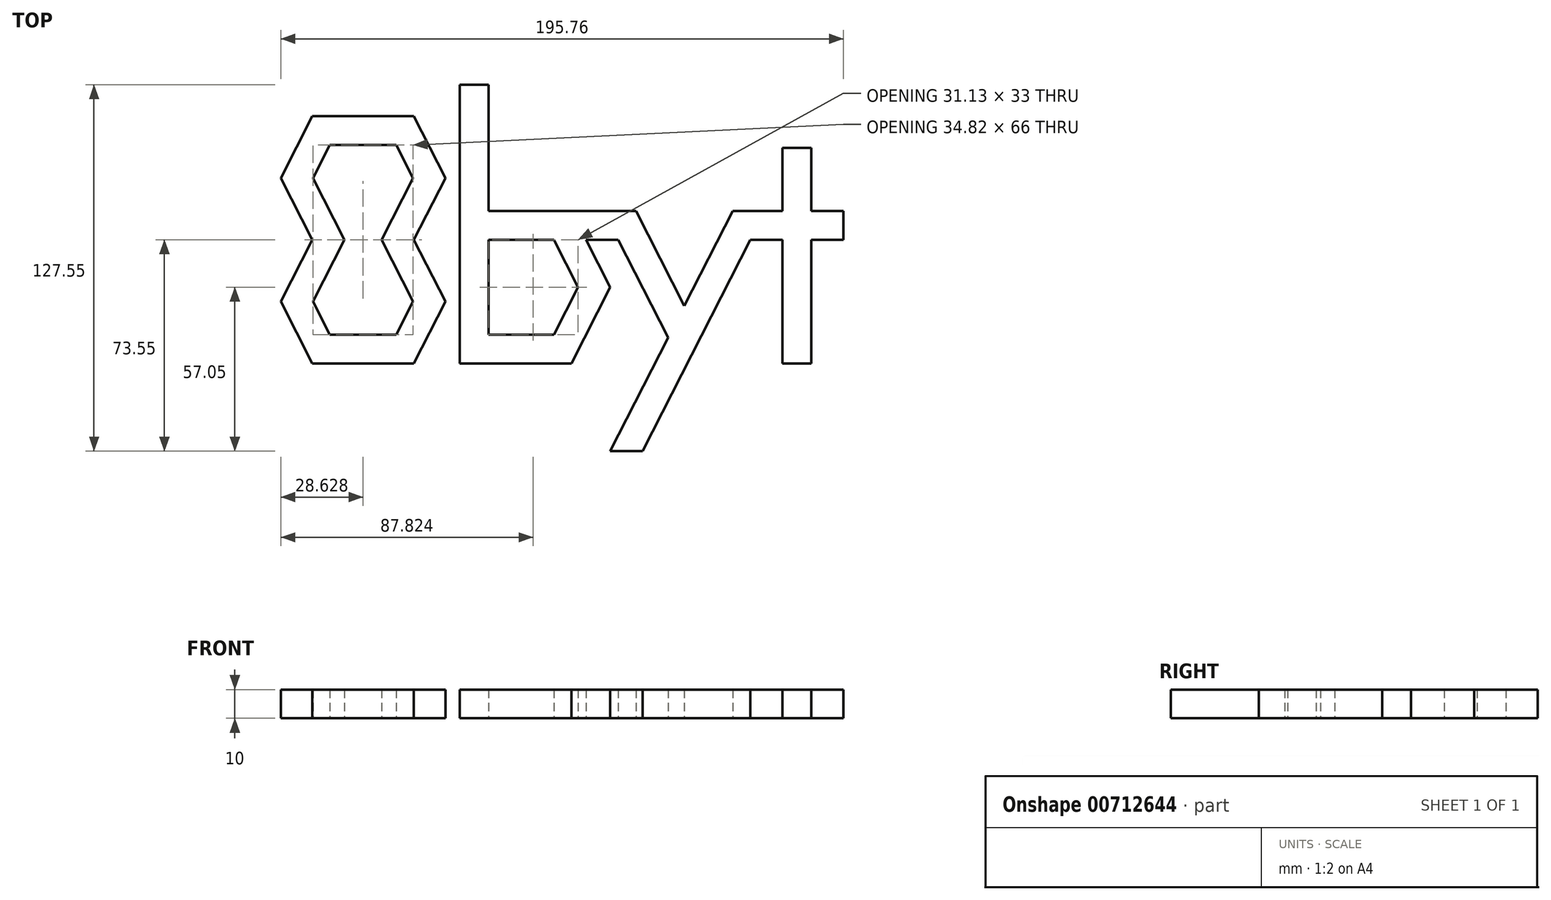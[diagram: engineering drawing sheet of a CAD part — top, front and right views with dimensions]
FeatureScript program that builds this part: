
annotation { "Feature Type Name" : "Feature", "Feature Type Description" : "" }
export const myFeature = defineFeature(function(context is Context, id is Id, definition is map)
    precondition{}
    {
        {
            var Q0;
            Q0=qCreatedBy(makeId("Top.planeOp"),FACE);
            var sketch = newSketch(context, id + "F0", { "sketchPlane" : qUnion([Q0])});
            skLineSegment(sketch, "E0", {"start": v(34.17, 32) * mm, "end": v(44.17, 32) * mm});
            skLineSegment(sketch, "E1", {"start": v(44.17, 32) * mm, "end": v(44.17, 10) * mm});
            skLineSegment(sketch, "E2", {"start": v(44.17, 10) * mm, "end": v(55.39, 10) * mm});
            skLineSegment(sketch, "E3", {"start": v(55.39, 10) * mm, "end": v(55.39, 0) * mm});
            skLineSegment(sketch, "E4", {"start": v(55.39, 0) * mm, "end": v(44.17, 0) * mm});
            skLineSegment(sketch, "E5", {"start": v(44.17, 0) * mm, "end": v(44.17, -43) * mm});
            skLineSegment(sketch, "E6", {"start": v(44.17, -43) * mm, "end": v(34.17, -43) * mm});
            skLineSegment(sketch, "E7", {"start": v(34.17, -43) * mm, "end": v(34.17, 0) * mm});
            skLineSegment(sketch, "E8", {"start": v(34.17, 0) * mm, "end": v(22.94, 0) * mm});
            skLineSegment(sketch, "E9", {"start": v(22.94, 0) * mm, "end": v(-14.54, -73.55) * mm});
            skLineSegment(sketch, "E10", {"start": v(-14.54, -73.55) * mm, "end": v(-25.76, -73.55) * mm});
            skLineSegment(sketch, "E11", {"start": v(-25.76, -73.55) * mm, "end": v(-5.61, -34.01) * mm});
            skLineSegment(sketch, "E12", {"start": v(-16.81, 10) * mm, "end": v(0, -23) * mm});
            skLineSegment(sketch, "E13", {"start": v(-5.61, -34.01) * mm, "end": v(-28.04, 10) * mm, "construction": true});
            skLineSegment(sketch, "E14", {"start": v(-16.81, 10) * mm, "end": v(-28.04, 10) * mm});
            skLineSegment(sketch, "E15", {"start": v(0, -23) * mm, "end": v(16.81, 10) * mm});
            skLineSegment(sketch, "E16", {"start": v(16.81, 10) * mm, "end": v(34.17, 10) * mm});
            skLineSegment(sketch, "E17", {"start": v(34.17, 10) * mm, "end": v(34.17, 32) * mm});
            skLineSegment(sketch, "E18", {"start": v(-22.94, 0) * mm, "end": v(-34.17, 0) * mm});
            skLineSegment(sketch, "E19", {"start": v(-34.17, 0) * mm, "end": v(-25.76, -16.5) * mm});
            skLineSegment(sketch, "E20", {"start": v(-25.76, -16.5) * mm, "end": v(-39.26, -43) * mm});
            skLineSegment(sketch, "E21", {"start": v(-39.26, -43) * mm, "end": v(-78.11, -43) * mm});
            skLineSegment(sketch, "E22", {"start": v(-78.11, 54) * mm, "end": v(-68.11, 54) * mm});
            skLineSegment(sketch, "E23", {"start": v(-68.11, 54) * mm, "end": v(-68.11, 10) * mm});
            skLineSegment(sketch, "E24", {"start": v(-68.11, 10) * mm, "end": v(-28.04, 10) * mm});
            skLineSegment(sketch, "E25", {"start": v(-39.26, -43) * mm, "end": v(34.17, -43) * mm, "construction": true});
            skLineSegment(sketch, "E26", {"start": v(-16.81, 10) * mm, "end": v(16.81, 10) * mm, "construction": true});
            skLineSegment(sketch, "E27", {"start": v(44.17, 10) * mm, "end": v(44.17, 0) * mm, "construction": true});
            skLineSegment(sketch, "E28", {"start": v(34.17, 0) * mm, "end": v(34.17, 10) * mm, "construction": true});
            skLineSegment(sketch, "E29", {"start": v(34.17, 10) * mm, "end": v(44.17, 10) * mm, "construction": true});
            skLineSegment(sketch, "E30", {"start": v(-15.69, -53.78) * mm, "end": v(-6.77, -58.32) * mm, "construction": true});
            skLineSegment(sketch, "E31", {"start": v(-8.4, -6.5) * mm, "end": v(-17.32, -11.04) * mm, "construction": true});
            skLineSegment(sketch, "E32", {"start": v(0, -23) * mm, "end": v(-5.61, -34.01) * mm, "construction": true});
            skLineSegment(sketch, "E33", {"start": v(-25.76, -16.5) * mm, "end": v(-78.11, -16.5) * mm, "construction": true});
            skLineSegment(sketch, "E34", {"start": v(-68.11, 10) * mm, "end": v(-78.11, 10) * mm, "construction": true});
            skLineSegment(sketch, "E35", {"start": v(-22.94, 0) * mm, "end": v(-5.61, -34.01) * mm});
            skLineSegment(sketch, "E36", {"start": v(-78.11, 10) * mm, "end": v(-78.11, -43) * mm});
            skLineSegment(sketch, "E37", {"start": v(-78.11, 10) * mm, "end": v(-78.11, 54) * mm});
            skLineSegment(sketch, "E38", {"start": v(-29.96, -8.25) * mm, "end": v(-21.05, -3.71) * mm, "construction": true});
            skLineSegment(sketch, "E39", {"start": v(-68.11, -33) * mm, "end": v(-45.39, -33) * mm});
            skLineSegment(sketch, "E40", {"start": v(-45.39, -33) * mm, "end": v(-36.98, -16.5) * mm});
            skLineSegment(sketch, "E41", {"start": v(-36.98, -16.5) * mm, "end": v(-45.39, 0) * mm});
            skLineSegment(sketch, "E42", {"start": v(-45.39, 0) * mm, "end": v(-68.11, 0) * mm});
            skLineSegment(sketch, "E43", {"start": v(-41.19, -8.25) * mm, "end": v(-32.28, -3.71) * mm, "construction": true});
            skLineSegment(sketch, "E44", {"start": v(-68.11, 10) * mm, "end": v(-68.11, 0) * mm, "construction": true});
            skLineSegment(sketch, "E45", {"start": v(-58.69, -43) * mm, "end": v(-58.69, -33) * mm, "construction": true});
            skLineSegment(sketch, "E46", {"start": v(-45.39, 0) * mm, "end": v(-63.9, 0) * mm, "construction": true});
            skLineSegment(sketch, "E47", {"start": v(-63.9, 0) * mm, "end": v(-72.31, -16.5) * mm, "construction": true});
            skLineSegment(sketch, "E48", {"start": v(-72.31, -16.5) * mm, "end": v(-63.9, -33) * mm, "construction": true});
            skLineSegment(sketch, "E49", {"start": v(-63.9, -33) * mm, "end": v(-45.39, -33) * mm, "construction": true});
            skLineSegment(sketch, "E50", {"start": v(34.17, 32) * mm, "end": v(-68.11, 32) * mm, "construction": true});
            skLineSegment(sketch, "E51", {"start": v(-68.11, 0) * mm, "end": v(-68.11, -16.5) * mm});
            skLineSegment(sketch, "E52", {"start": v(-68.11, -16.5) * mm, "end": v(-68.11, -33) * mm});
            skPoint(sketch, "E53", {"position": v(-68.11, -8.25) * mm});
            skLineSegment(sketch, "E54", {"start": v(-78.11, -43) * mm, "end": v(-94.07, -43) * mm, "construction": true});
            skLineSegment(sketch, "E55", {"start": v(-94.07, -43) * mm, "end": v(-129.42, -43) * mm});
            skLineSegment(sketch, "E56", {"start": v(-129.42, -43) * mm, "end": v(-140.37, -21.5) * mm});
            skLineSegment(sketch, "E57", {"start": v(-140.37, -21.5) * mm, "end": v(-129.42, 0) * mm});
            skLineSegment(sketch, "E58", {"start": v(-129.42, 0) * mm, "end": v(-140.37, 21.5) * mm});
            skLineSegment(sketch, "E59", {"start": v(-140.37, 21.5) * mm, "end": v(-129.42, 43) * mm});
            skLineSegment(sketch, "E60", {"start": v(-129.42, 43) * mm, "end": v(-94.07, 43) * mm});
            skLineSegment(sketch, "E61", {"start": v(-94.07, 43) * mm, "end": v(-83.11, 21.5) * mm});
            skLineSegment(sketch, "E62", {"start": v(-83.11, 21.5) * mm, "end": v(-94.07, 0) * mm});
            skLineSegment(sketch, "E63", {"start": v(-94.07, 0) * mm, "end": v(-83.11, -21.5) * mm});
            skLineSegment(sketch, "E64", {"start": v(-83.11, -21.5) * mm, "end": v(-94.07, -43) * mm});
            skLineSegment(sketch, "E65", {"start": v(-78.11, 32) * mm, "end": v(-78.11, 54) * mm, "construction": true});
            skLineSegment(sketch, "E66", {"start": v(-78.11, 43) * mm, "end": v(-94.07, 43) * mm, "construction": true});
            skLineSegment(sketch, "E67", {"start": v(-129.15, 21.5) * mm, "end": v(-123.3, 33) * mm});
            skLineSegment(sketch, "E68", {"start": v(-123.3, 33) * mm, "end": v(-100.2, 33) * mm});
            skLineSegment(sketch, "E69", {"start": v(-100.2, 33) * mm, "end": v(-94.33, 21.5) * mm});
            skLineSegment(sketch, "E70", {"start": v(-94.33, 21.5) * mm, "end": v(-105.29, 0) * mm});
            skLineSegment(sketch, "E71", {"start": v(-105.29, 0) * mm, "end": v(-94.33, -21.5) * mm});
            skLineSegment(sketch, "E72", {"start": v(-94.33, -21.5) * mm, "end": v(-100.2, -33) * mm});
            skLineSegment(sketch, "E73", {"start": v(-100.2, -33) * mm, "end": v(-123.3, -33) * mm});
            skLineSegment(sketch, "E74", {"start": v(-123.3, -33) * mm, "end": v(-129.15, -21.5) * mm});
            skLineSegment(sketch, "E75", {"start": v(-129.15, -21.5) * mm, "end": v(-118.2, 0) * mm});
            skLineSegment(sketch, "E76", {"start": v(-118.2, 0) * mm, "end": v(-129.15, 21.5) * mm});
            skLineSegment(sketch, "E77", {"start": v(-111.74, -33) * mm, "end": v(-111.74, -43) * mm, "construction": true});
            skLineSegment(sketch, "E78", {"start": v(-97.5, -27.71) * mm, "end": v(-88.59, -32.25) * mm, "construction": true});
            skLineSegment(sketch, "E79", {"start": v(-97.5, -15.29) * mm, "end": v(-88.59, -10.75) * mm, "construction": true});
            skLineSegment(sketch, "E80", {"start": v(-125.99, -27.71) * mm, "end": v(-134.9, -32.25) * mm, "construction": true});
            skLineSegment(sketch, "E81", {"start": v(-125.99, -15.29) * mm, "end": v(-134.9, -10.75) * mm, "construction": true});
            skLineSegment(sketch, "E82", {"start": v(-125.99, 15.29) * mm, "end": v(-134.9, 10.75) * mm, "construction": true});
            skLineSegment(sketch, "E83", {"start": v(-126.22, 27.25) * mm, "end": v(-135.13, 31.79) * mm, "construction": true});
            skLineSegment(sketch, "E84", {"start": v(-111.74, 33) * mm, "end": v(-111.74, 43) * mm, "construction": true});
            skLineSegment(sketch, "E85", {"start": v(-97.26, 27.25) * mm, "end": v(-88.35, 31.79) * mm, "construction": true});
            skLineSegment(sketch, "E86", {"start": v(-97.5, 15.29) * mm, "end": v(-88.59, 10.75) * mm, "construction": true});
            skLineSegment(sketch, "E87", {"start": v(-105.29, 0) * mm, "end": v(-118.2, 0) * mm, "construction": true});
            skLineSegment(sketch, "E88", {"start": v(-78.11, -31.31) * mm, "end": v(-88.11, -31.31) * mm, "construction": true});
            skLineSegment(sketch, "E89", {"start": v(-83.11, -21.5) * mm, "end": v(-83.11, -31.31) * mm, "construction": true});
            skLineSegment(sketch, "E90", {"start": v(-25.76, -73.55) * mm, "end": v(-25.76, -16.5) * mm, "construction": true});
            skSolve(sketch);
        }
        {
            var Q0;
            Q0 = qSketchRegion(id + "F0", true);
            extrude(context, id + "F1", {"entities" : qUnion([Q0]), "depth" : 10 * mm, "offsetDistance" : 25 * mm});
        }
    });
